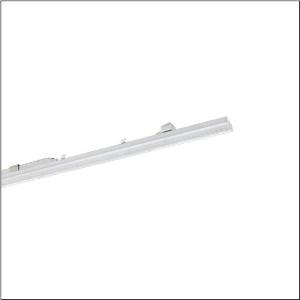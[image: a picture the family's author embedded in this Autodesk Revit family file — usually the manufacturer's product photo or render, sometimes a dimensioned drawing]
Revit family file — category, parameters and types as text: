
# Revit family: tl_l_5wd7a8d0a2c5
name_source: partatom
category: Lighting Fixtures
units: mm (PartAtom-declared; Revit-internal decimal feet)

## family parameters
Cut with Voids When Loaded = No
Host = Face
Light Source = No
Part Type = Normal
Room Calculation Point = No
Round Connector Dimension = Use Diameter
Shared = No

## types (1)
- --- (1 x LED, 9800 lm, 63.3 W, 4000K)
    Apparent Load = 63 VA
    CIE Flux Codes = 49 84 98 100 100
    Color Rendering = 80
    Color Temperature = 4000K
    Default Elevation = 1800 mm
    Description = TL L, luminaire insert, of sheet steel, galvanised, coil coated, white, length: 1.500mm, width: 66mm, height: 67mm, LED rated luminous flux: 9.800lm, light colour: 840, control gear: DALI, with terminal, 5-pole, mains connection: 230..240V, AC, 50/60Hz, rated input power: 63W, primary optical cover: cover, of PMMA, light emission: direct distribution, protection rating (complete): as luminaire, insulation class (complete): insulation class I (protective earthing), certification: CE, impact resistance: IK06, permissible ambient temperature for indoor applications: -25..+35°C, packaging unit: 1 piece
    Height = 120 mm
    Lamp = 1 x LED
    Lamp Light Flux = 9800 lm
    Lamp Power = 63.3 W
    Lamp count = 1
    Length = 1690 mm
    Luminous efficacy = 155 lm/W
    Manufacturer = Siteco
    ModVariant = No
    Model = 5WD7A8D0A2C5
    Mounting Place = Ceiling
    Mounting Type = Pendant
    Number of Poles = 1
    OnlyDefault = Yes
    Power Factor = 1
    Product Name = TL L
    Product group = luminaire insert
    ProductGroupID = 901
    Protection Class = Protection class I
    Protection Degree = Degree of protection
    RLX_Detail_Level = 1
    RLX_Emergency_Light_Flux = 0 lm
    RLX_Emergency_Type = 0
    RLX_Emergency_Type_DB = No
    RlxData = <blob elided: 17317 chars, md5=52a39f35>
    Socket = socket
    Standby Power = 0 W
    System Light Flux = 9800 lm
    System Power = 63 W
    Type Comments = factory setting: luminous flux: 100 % | dim-lin: 254 | 420 mA
    Type Image = l_1294382.jpg
    URL = http://relux.com
    VarID = @adj_012549
    Voltage = 0 V
    Weight = 0.00 kg
    Width = 208 mm

## geometry (parser evidence)
native form markers: Blend x4, Sweep x9
no freeform markers — native parametric forms only
